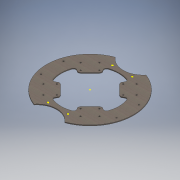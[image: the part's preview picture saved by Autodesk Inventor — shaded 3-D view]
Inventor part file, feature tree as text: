
AUTODESK INVENTOR PART (.ipt)
format: ipt  version: 2020 (Build 240168000, 168)  size: 367,616 bytes
history: native  units: mm
features: other x4, sketch x4, extrude x3, projected_geometry x2, fillet x1
ambient origin geometry x8: Origin, YZ Plane, XZ Plane, XY Plane, X Axis, Y Axis, Z Axis, Center Point
bodies: Body1 (feature_tree)
feature tree (14):
  other  "floor_v2.ipt"
  sketch  "Эскиз1"
  extrude  "Выдавливание1"  Depth=10.0mm
  fillet  "Сопряжение1"  Radius=6.0mm
  sketch  "Эскиз2"
  extrude  "Выдавливание2"  Depth=6.0mm
  sketch  "Эскиз3"
  extrude  "Выдавливание3"  Depth=6.0mm
  other  "Твердое тело1::floor_v2.ipt"
  other  "Элемент создания тегов1"
  projected_geometry  "Спроецированная петля1"
  sketch  "Эскиз4"
  projected_geometry  "Спроецированная петля2"
  other  "Твердое тело1"
